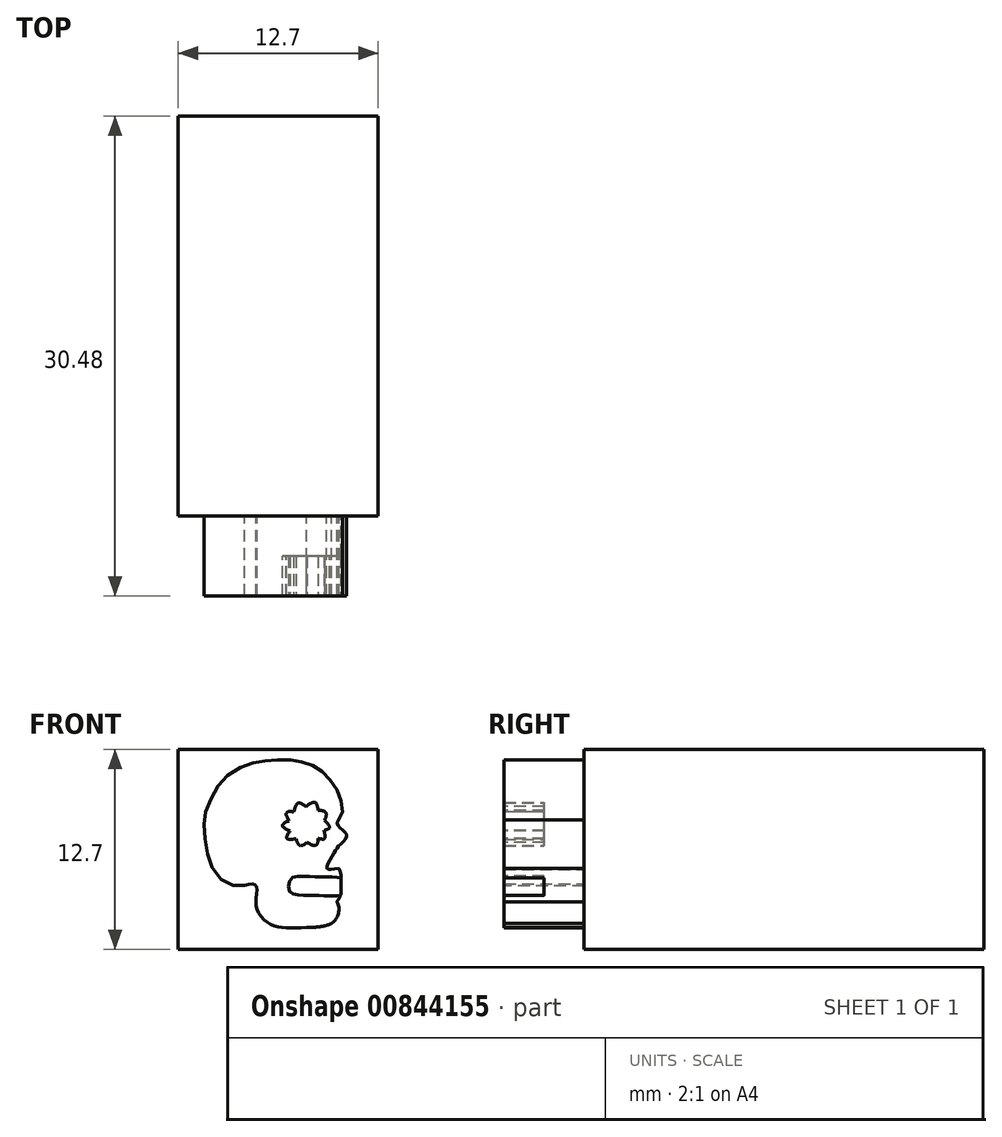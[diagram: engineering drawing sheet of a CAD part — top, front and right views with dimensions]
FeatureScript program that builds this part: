
annotation { "Feature Type Name" : "Feature", "Feature Type Description" : "" }
export const myFeature = defineFeature(function(context is Context, id is Id, definition is map)
    precondition{}
    {
        {
            var Q0;
            Q0=qCreatedBy(makeId("Front.planeOp"),FACE);
            var sketch = newSketch(context, id + "F0", { "sketchPlane" : qUnion([Q0])});
            skArc(sketch, "E0", {"start": v(-2.96, 1.65) * mm, "mid": v(-2.52, 2.28) * mm, "end": v(-2.62, 3.03) * mm});
            skFitSpline(sketch, "E1", {"points": [v(-4.55, 1.4) * mm, v(-2.96, 1.65) * mm], "startDerivative": vector(1.7, 0) * mm, "endDerivative": vector(1.51, 0.7) * mm});
            skFitSpline(sketch, "E2", {"points": [v(-2.49, 5.13) * mm, v(-2.35, 4.58) * mm, v(-2.35, 4.15) * mm, v(-2.35, 3.77) * mm, v(-2.62, 3.03) * mm], "startDerivative": vector(1.13, -2.5) * mm, "endDerivative": vector(-2.25, -2.73) * mm});
            skFitSpline(sketch, "E3", {"points": [v(-8.49, 4.08) * mm, v(-9.32, 4.08) * mm, v(-10.36, 4.88) * mm, v(-10.86, 6.14) * mm, v(-11.05, 7.58) * mm, v(-10.98, 8.64) * mm, v(-10.5, 9.83) * mm, v(-9.7, 10.94) * mm, v(-8.49, 11.66) * mm, v(-7.5, 11.93) * mm, v(-6.53, 12.03) * mm, v(-5.49, 12.02) * mm, v(-4.7, 11.87) * mm, v(-3.86, 11.55) * mm, v(-3.27, 11.01) * mm, v(-2.68, 10.28) * mm, v(-2.36, 9.45) * mm, v(-2.28, 8.68) * mm, v(-2.5, 8.22) * mm], "startDerivative": vector(-16.18, -2.66) * mm, "endDerivative": vector(-3.8, -12.82) * mm});
            skFitSpline(sketch, "E4", {"points": [v(-2.49, 5.13) * mm, v(-3.25, 5.13) * mm, v(-2.88, 5.99) * mm, v(-2.49, 6.59) * mm, v(-2, 7.19) * mm, v(-2.35, 7.65) * mm, v(-2.5, 8.22) * mm], "startDerivative": vector(-6.38, 0.02) * mm, "endDerivative": vector(4.2, 4.48) * mm});
            skFitSpline(sketch, "E5", {"points": [v(-8.49, 4.08) * mm, v(-7.77, 4.08) * mm, v(-7.74, 3.33) * mm, v(-7.65, 2.44) * mm, v(-6.94, 1.64) * mm, v(-6.06, 1.39) * mm, v(-4.55, 1.4) * mm], "startDerivative": vector(6.23, 1.32) * mm, "endDerivative": vector(7.7, 0.3) * mm});
            skSolve(sketch);
        }
        {
            var Q0;
            Q0=qCreatedBy(makeId("Front.planeOp"),FACE);
            var sketch = newSketch(context, id + "F1", { "sketchPlane" : qUnion([Q0])});
            skLineSegment(sketch, "E6.bottom", {"start": v(0, 0) * mm, "end": v(-12.7, 0) * mm});
            skLineSegment(sketch, "E6.top", {"start": v(0, 12.7) * mm, "end": v(-12.7, 12.7) * mm});
            skLineSegment(sketch, "E6.left", {"start": v(0, 0) * mm, "end": v(0, 12.7) * mm});
            skLineSegment(sketch, "E6.right", {"start": v(-12.7, 0) * mm, "end": v(-12.7, 12.7) * mm});
            skSolve(sketch);
        }
        {
            var Q0;
            Q0 = qSketchRegion(id + "F0", true);
            extrude(context, id + "F2", {"entities" : qUnion([Q0]), "depth" : 5.08 * mm, "offsetDistance" : 25.4 * mm});
        }
        {
            var Q0;
            Q0=makeQuery(id+"F2.opExtrude","CAP_FACE",FACE,{"disambiguationData":[OSD([sQuery(id+"F0.wireOp",EDGE,"E0"),sQuery(id+"F0.wireOp",EDGE,"E1"),sQuery(id+"F0.wireOp",EDGE,"E2"),sQuery(id+"F0.wireOp",EDGE,"E3"),sQuery(id+"F0.wireOp",EDGE,"E4"),sQuery(id+"F0.wireOp",EDGE,"E5")])],"isStart":false});
            var sketch = newSketch(context, id + "F3", { "sketchPlane" : qUnion([Q0])});
            skFitSpline(sketch, "E7", {"points": [v(-5.37, 8.72) * mm, v(-5.09, 9.3) * mm, v(-4.59, 9.09) * mm], "startDerivative": vector(0.47, 1.45) * mm, "endDerivative": vector(1.15, -0.78) * mm});
            skFitSpline(sketch, "E8", {"points": [v(-4.59, 9.09) * mm, v(-4, 9.34) * mm, v(-3.8, 8.84) * mm], "startDerivative": vector(1.32, 0.85) * mm, "endDerivative": vector(0.23, -1.41) * mm});
            skFitSpline(sketch, "E9", {"points": [v(-3.8, 8.84) * mm, v(-3.33, 8.7) * mm, v(-3.4, 8.2) * mm], "startDerivative": vector(1.47, -0.06) * mm, "endDerivative": vector(-0.68, -1.2) * mm});
            skFitSpline(sketch, "E10", {"points": [v(-3.4, 8.2) * mm, v(-3.09, 7.74) * mm, v(-3.45, 7.56) * mm], "startDerivative": vector(0.96, -0.98) * mm, "endDerivative": vector(-1.07, -0.3) * mm});
            skFitSpline(sketch, "E11", {"points": [v(-3.45, 7.56) * mm, v(-3.4, 7.03) * mm, v(-3.8, 7.05) * mm], "startDerivative": vector(0.3, -1.24) * mm, "endDerivative": vector(-1.07, 0.2) * mm});
            skFitSpline(sketch, "E12", {"points": [v(-3.8, 7.05) * mm, v(-3.96, 6.61) * mm, v(-4.5, 6.8) * mm], "startDerivative": vector(-0.06, -1.45) * mm, "endDerivative": vector(-1.31, 0.89) * mm});
            skFitSpline(sketch, "E13", {"points": [v(-4.5, 6.8) * mm, v(-4.97, 6.6) * mm, v(-5.2, 7.02) * mm], "startDerivative": vector(-1.11, -0.95) * mm, "endDerivative": vector(-0.36, 1.4) * mm});
            skFitSpline(sketch, "E14", {"points": [v(-5.2, 7.02) * mm, v(-5.8, 7.05) * mm, v(-5.6, 7.52) * mm], "startDerivative": vector(-1.8, -0.17) * mm, "endDerivative": vector(1.04, 1.25) * mm});
            skFitSpline(sketch, "E15", {"points": [v(-5.6, 7.52) * mm, v(-6.08, 7.87) * mm, v(-5.65, 8.17) * mm], "startDerivative": vector(-1.95, 0.8) * mm, "endDerivative": vector(1.88, 0.54) * mm});
            skFitSpline(sketch, "E16", {"points": [v(-5.65, 8.17) * mm, v(-5.82, 8.67) * mm, v(-5.37, 8.72) * mm], "startDerivative": vector(-1.13, 1.61) * mm, "endDerivative": vector(1.77, -0.5) * mm});
            skFitSpline(sketch, "E17", {"points": [v(-2.34, 4.55) * mm, v(-3.26, 4.6) * mm, v(-4.47, 4.63) * mm, v(-5.54, 4.49) * mm, v(-5.6, 3.64) * mm, v(-4.72, 3.45) * mm, v(-3.7, 3.42) * mm, v(-2.9, 3.4) * mm, v(-2.4, 3.42) * mm], "startDerivative": vector(-5.62, 0.65) * mm, "endDerivative": vector(4.79, 0.23) * mm});
            skSolve(sketch);
        }
        {
            var Q0;
            Q0=makeQuery(id+"F3.imprint","IMPRINT",FACE,{"disambiguationData":[TD([[makeQuery(id+"F3.imprint","IMPRINT",EDGE,{"derivedFrom":sQuery(id+"F3.wireOp",EDGE,"E7")}),-1.0]])]});
            var Q1;
            {var subQ0=sQuery(id+"F3.wireOp",EDGE,"E17");Q1=makeQuery(id+"F3.imprint","IMPRINT",FACE,{"disambiguationData":[TD([[makeQuery(id+"F3.imprint","IMPRINT",EDGE,{"derivedFrom":subQ0}),1.0]])]});}
            extrude(context, id + "F4", {"entities" : qUnion([Q0, Q1]), "operationType" : NewBodyOperationType.REMOVE, "oppositeDirection" : true, "depth" : 2.54 * mm, "offsetDistance" : 25.4 * mm});
        }
        {
            var Q0;
            Q0 = qSketchRegion(id + "F1", true);
            extrude(context, id + "F5", {"entities" : qUnion([Q0]), "operationType" : NewBodyOperationType.ADD, "oppositeDirection" : true, "depth" : 25.4 * mm, "offsetDistance" : 25.4 * mm});
        }
    });
